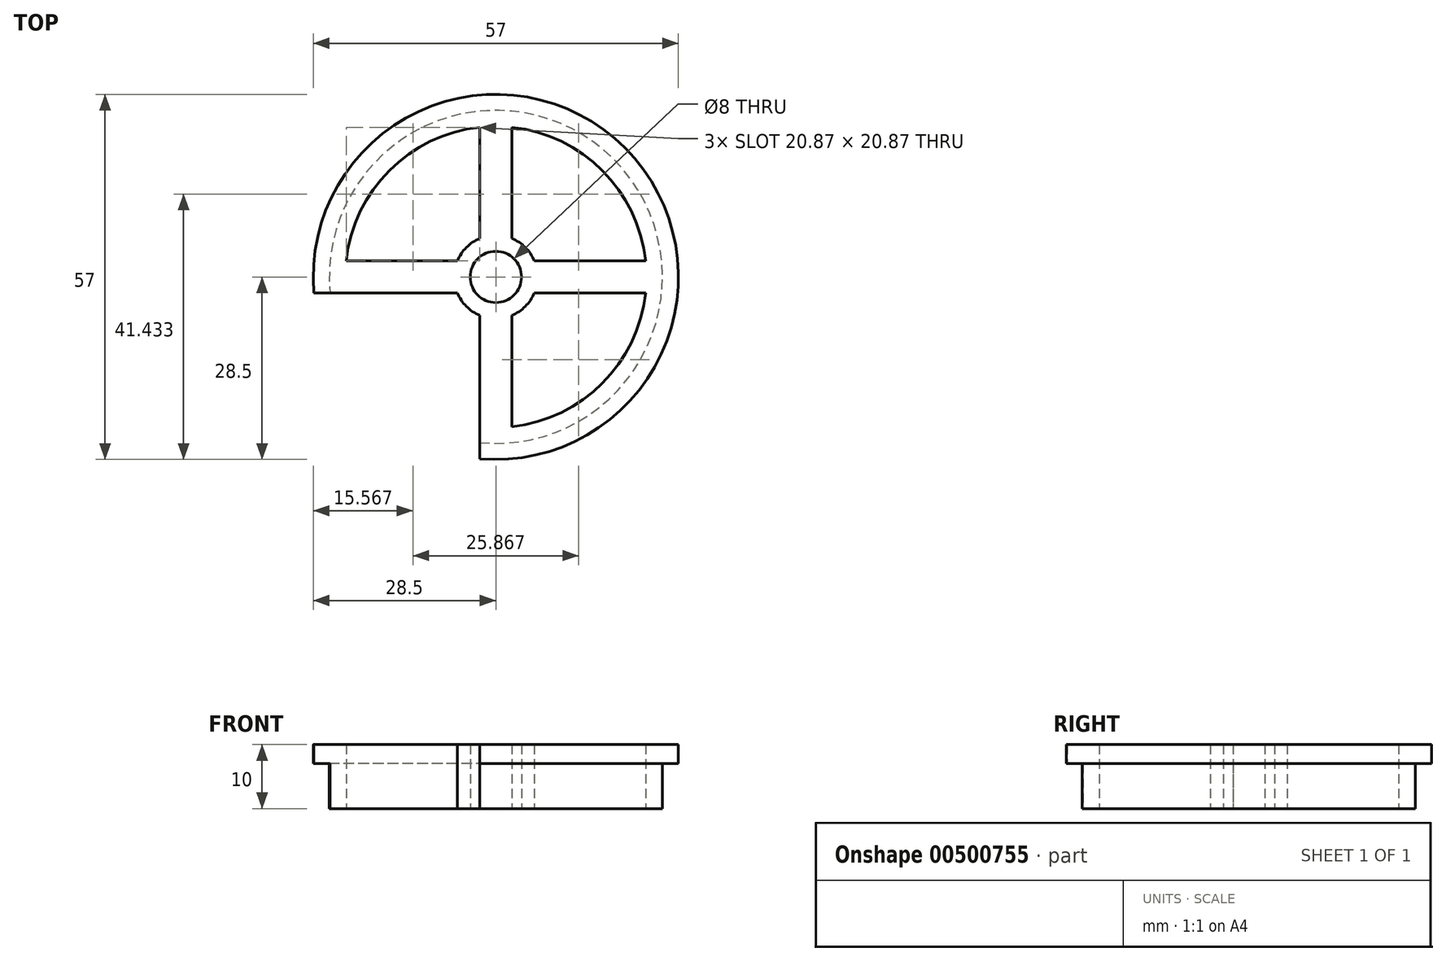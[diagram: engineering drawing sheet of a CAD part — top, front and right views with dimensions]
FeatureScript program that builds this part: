
annotation { "Feature Type Name" : "Feature", "Feature Type Description" : "" }
export const myFeature = defineFeature(function(context is Context, id is Id, definition is map)
    precondition{}
    {
        {
            var Q0;
            Q0=qCreatedBy(makeId("Top.planeOp"),FACE);
            var sketch = newSketch(context, id + "F0", { "sketchPlane" : qUnion([Q0])});
            skCircle(sketch, "E0", {"center": v(0, 0) * mm, "radius": 4 * mm});
            skCircle(sketch, "E1", {"center": v(0, 0) * mm, "radius": 26 * mm});
            skCircle(sketch, "E2", {"center": v(0, 0) * mm, "radius": 28.5 * mm});
            skCircle(sketch, "E3", {"center": v(0, 0) * mm, "radius": 6.5 * mm});
            skLineSegment(sketch, "E4.bottom", {"start": v(-2.5, 36.95) * mm, "end": v(2.5, 36.95) * mm});
            skLineSegment(sketch, "E4.top", {"start": v(-2.5, -38.22) * mm, "end": v(2.5, -38.22) * mm});
            skLineSegment(sketch, "E4.left", {"start": v(-2.5, 36.95) * mm, "end": v(-2.5, -38.22) * mm});
            skLineSegment(sketch, "E4.right", {"start": v(2.5, 36.95) * mm, "end": v(2.5, -38.22) * mm});
            skLineSegment(sketch, "E5.bottom", {"start": v(-35.79, 2.5) * mm, "end": v(49.49, 2.5) * mm});
            skLineSegment(sketch, "E5.top", {"start": v(-35.79, -2.5) * mm, "end": v(49.49, -2.5) * mm});
            skLineSegment(sketch, "E5.left", {"start": v(-35.79, 2.5) * mm, "end": v(-35.79, -2.5) * mm});
            skLineSegment(sketch, "E5.right", {"start": v(49.49, 2.5) * mm, "end": v(49.49, -2.5) * mm});
            skCircle(sketch, "E6", {"center": v(0, 0) * mm, "radius": 23.5 * mm});
            skSolve(sketch);
        }
        {
            var Q0;
            {var subQ0=sQuery(id+"F0.wireOp",EDGE,"E5.bottom");var subQ1=sQuery(id+"F0.wireOp",EDGE,"E1");var subQ2=makeQuery(id+"F0.imprint","INTERSECT",VERTEX,{"disambiguationData":[OD(0.0)],"derivedFrom":[subQ1,subQ0]});Q0=makeQuery(id+"F0.imprint","IMPRINT",FACE,{"disambiguationData":[TD([[makeQuery(id+"F0.imprint","IMPRINT",EDGE,{"disambiguationData":[TD([[subQ2,1.0]])],"derivedFrom":subQ1}),1.0]])]});}
            var Q1;
            {var subQ0=sQuery(id+"F0.wireOp",EDGE,"E5.bottom");var subQ1=sQuery(id+"F0.wireOp",EDGE,"E3");var subQ2=makeQuery(id+"F0.imprint","INTERSECT",VERTEX,{"disambiguationData":[OD(0.0)],"derivedFrom":[subQ1,subQ0]});Q1=makeQuery(id+"F0.imprint","IMPRINT",FACE,{"disambiguationData":[TD([[makeQuery(id+"F0.imprint","IMPRINT",EDGE,{"disambiguationData":[TD([[subQ2,1.0]])],"derivedFrom":subQ1}),-1.0]])]});}
            var Q2;
            {var subQ0=sQuery(id+"F0.wireOp",EDGE,"E4.right");var subQ1=sQuery(id+"F0.wireOp",EDGE,"E1");var subQ2=makeQuery(id+"F0.imprint","INTERSECT",VERTEX,{"disambiguationData":[OD(0.0)],"derivedFrom":[subQ1,subQ0]});Q2=makeQuery(id+"F0.imprint","IMPRINT",FACE,{"disambiguationData":[TD([[makeQuery(id+"F0.imprint","IMPRINT",EDGE,{"disambiguationData":[TD([[subQ2,1.0]])],"derivedFrom":subQ1}),1.0]])]});}
            var Q3;
            {var subQ0=sQuery(id+"F0.wireOp",EDGE,"E4.left");var subQ1=sQuery(id+"F0.wireOp",EDGE,"E1");var subQ2=makeQuery(id+"F0.imprint","INTERSECT",VERTEX,{"disambiguationData":[OD(0.0)],"derivedFrom":[subQ1,subQ0]});Q3=makeQuery(id+"F0.imprint","IMPRINT",FACE,{"disambiguationData":[TD([[makeQuery(id+"F0.imprint","IMPRINT",EDGE,{"disambiguationData":[TD([[subQ2,-1.0]])],"derivedFrom":subQ1}),1.0]])]});}
            var Q4;
            {var subQ0=sQuery(id+"F0.wireOp",EDGE,"E4.right");var subQ1=sQuery(id+"F0.wireOp",EDGE,"E1");var subQ2=makeQuery(id+"F0.imprint","INTERSECT",VERTEX,{"disambiguationData":[OD(0.0)],"derivedFrom":[subQ1,subQ0]});Q4=makeQuery(id+"F0.imprint","IMPRINT",FACE,{"disambiguationData":[TD([[makeQuery(id+"F0.imprint","IMPRINT",EDGE,{"disambiguationData":[TD([[subQ2,-1.0]])],"derivedFrom":subQ1}),1.0]])]});}
            var Q5;
            {var subQ0=sQuery(id+"F0.wireOp",EDGE,"E5.bottom");var subQ1=sQuery(id+"F0.wireOp",EDGE,"E1");var subQ2=makeQuery(id+"F0.imprint","INTERSECT",VERTEX,{"disambiguationData":[OD(1.0)],"derivedFrom":[subQ1,subQ0]});Q5=makeQuery(id+"F0.imprint","IMPRINT",FACE,{"disambiguationData":[TD([[makeQuery(id+"F0.imprint","IMPRINT",EDGE,{"disambiguationData":[TD([[subQ2,-1.0]])],"derivedFrom":subQ1}),1.0]])]});}
            var Q6;
            {var subQ0=sQuery(id+"F0.wireOp",EDGE,"E5.top");var subQ1=sQuery(id+"F0.wireOp",EDGE,"E1");var subQ2=makeQuery(id+"F0.imprint","INTERSECT",VERTEX,{"disambiguationData":[OD(0.0)],"derivedFrom":[subQ1,subQ0]});Q6=makeQuery(id+"F0.imprint","IMPRINT",FACE,{"disambiguationData":[TD([[makeQuery(id+"F0.imprint","IMPRINT",EDGE,{"disambiguationData":[TD([[subQ2,-1.0]])],"derivedFrom":subQ1}),1.0]])]});}
            var Q7;
            {var subQ0=sQuery(id+"F0.wireOp",EDGE,"E4.left");var subQ1=sQuery(id+"F0.wireOp",EDGE,"E1");var subQ2=makeQuery(id+"F0.imprint","INTERSECT",VERTEX,{"disambiguationData":[OD(1.0)],"derivedFrom":[subQ1,subQ0]});Q7=makeQuery(id+"F0.imprint","IMPRINT",FACE,{"disambiguationData":[TD([[makeQuery(id+"F0.imprint","IMPRINT",EDGE,{"disambiguationData":[TD([[subQ2,-1.0]])],"derivedFrom":subQ1}),1.0]])]});}
            var Q8;
            {var subQ0=sQuery(id+"F0.wireOp",EDGE,"E4.right");var subQ1=sQuery(id+"F0.wireOp",EDGE,"E1");var subQ2=makeQuery(id+"F0.imprint","INTERSECT",VERTEX,{"disambiguationData":[OD(1.0)],"derivedFrom":[subQ1,subQ0]});Q8=makeQuery(id+"F0.imprint","IMPRINT",FACE,{"disambiguationData":[TD([[makeQuery(id+"F0.imprint","IMPRINT",EDGE,{"disambiguationData":[TD([[subQ2,-1.0]])],"derivedFrom":subQ1}),1.0]])]});}
            var Q9;
            {var subQ0=sQuery(id+"F0.wireOp",EDGE,"E5.bottom");var subQ1=sQuery(id+"F0.wireOp",EDGE,"E3");var subQ2=makeQuery(id+"F0.imprint","INTERSECT",VERTEX,{"disambiguationData":[OD(1.0)],"derivedFrom":[subQ1,subQ0]});Q9=makeQuery(id+"F0.imprint","IMPRINT",FACE,{"disambiguationData":[TD([[makeQuery(id+"F0.imprint","IMPRINT",EDGE,{"disambiguationData":[TD([[subQ2,-1.0]])],"derivedFrom":subQ1}),-1.0]])]});}
            var Q10;
            {var subQ0=sQuery(id+"F0.wireOp",EDGE,"E4.left");var subQ1=sQuery(id+"F0.wireOp",EDGE,"E0");var subQ5=makeQuery(id+"F0.imprint","INTERSECT",VERTEX,{"disambiguationData":[OD(0.0)],"derivedFrom":[subQ1,subQ0]});Q10=makeQuery(id+"F0.imprint","IMPRINT",FACE,{"disambiguationData":[TD([[makeQuery(id+"F0.imprint","IMPRINT",EDGE,{"disambiguationData":[TD([[subQ5,-1.0]])],"derivedFrom":subQ1}),-1.0]])]});}
            var Q11;
            {var subQ3=sQuery(id+"F0.wireOp",EDGE,"E5.bottom");var subQ8=sQuery(id+"F0.wireOp",EDGE,"E0");var subQ9=makeQuery(id+"F0.imprint","INTERSECT",VERTEX,{"disambiguationData":[OD(0.0)],"derivedFrom":[subQ8,subQ3]});Q11=makeQuery(id+"F0.imprint","IMPRINT",FACE,{"disambiguationData":[TD([[makeQuery(id+"F0.imprint","IMPRINT",EDGE,{"disambiguationData":[TD([[subQ9,-1.0]])],"derivedFrom":subQ8}),-1.0]])]});}
            var Q12;
            {var subQ0=sQuery(id+"F0.wireOp",EDGE,"E4.left");var subQ1=sQuery(id+"F0.wireOp",EDGE,"E3");var subQ2=makeQuery(id+"F0.imprint","INTERSECT",VERTEX,{"disambiguationData":[OD(1.0)],"derivedFrom":[subQ1,subQ0]});Q12=makeQuery(id+"F0.imprint","IMPRINT",FACE,{"disambiguationData":[TD([[makeQuery(id+"F0.imprint","IMPRINT",EDGE,{"disambiguationData":[TD([[subQ2,-1.0]])],"derivedFrom":subQ1}),-1.0]])]});}
            var Q13;
            {var subQ0=sQuery(id+"F0.wireOp",EDGE,"E4.right");var subQ1=sQuery(id+"F0.wireOp",EDGE,"E0");var subQ9=makeQuery(id+"F0.imprint","INTERSECT",VERTEX,{"disambiguationData":[OD(0.0)],"derivedFrom":[subQ1,subQ0]});Q13=makeQuery(id+"F0.imprint","IMPRINT",FACE,{"disambiguationData":[TD([[makeQuery(id+"F0.imprint","IMPRINT",EDGE,{"disambiguationData":[TD([[subQ9,1.0]])],"derivedFrom":subQ1}),-1.0]])]});}
            var Q14;
            {var subQ0=sQuery(id+"F0.wireOp",EDGE,"E4.right");var subQ1=sQuery(id+"F0.wireOp",EDGE,"E3");var subQ2=makeQuery(id+"F0.imprint","INTERSECT",VERTEX,{"disambiguationData":[OD(1.0)],"derivedFrom":[subQ1,subQ0]});Q14=makeQuery(id+"F0.imprint","IMPRINT",FACE,{"disambiguationData":[TD([[makeQuery(id+"F0.imprint","IMPRINT",EDGE,{"disambiguationData":[TD([[subQ2,-1.0]])],"derivedFrom":subQ1}),1.0]])]});}
            var Q15;
            {var subQ3=sQuery(id+"F0.wireOp",EDGE,"E5.top");var subQ8=sQuery(id+"F0.wireOp",EDGE,"E0");var subQ9=makeQuery(id+"F0.imprint","INTERSECT",VERTEX,{"disambiguationData":[OD(0.0)],"derivedFrom":[subQ8,subQ3]});Q15=makeQuery(id+"F0.imprint","IMPRINT",FACE,{"disambiguationData":[TD([[makeQuery(id+"F0.imprint","IMPRINT",EDGE,{"disambiguationData":[TD([[subQ9,-1.0]])],"derivedFrom":subQ8}),-1.0]])]});}
            var Q16;
            {var subQ0=sQuery(id+"F0.wireOp",EDGE,"E5.top");var subQ1=sQuery(id+"F0.wireOp",EDGE,"E3");var subQ2=makeQuery(id+"F0.imprint","INTERSECT",VERTEX,{"disambiguationData":[OD(0.0)],"derivedFrom":[subQ1,subQ0]});Q16=makeQuery(id+"F0.imprint","IMPRINT",FACE,{"disambiguationData":[TD([[makeQuery(id+"F0.imprint","IMPRINT",EDGE,{"disambiguationData":[TD([[subQ2,-1.0]])],"derivedFrom":subQ1}),1.0]])]});}
            var Q17;
            {var subQ0=sQuery(id+"F0.wireOp",EDGE,"E4.left");var subQ1=sQuery(id+"F0.wireOp",EDGE,"E3");var subQ2=makeQuery(id+"F0.imprint","INTERSECT",VERTEX,{"disambiguationData":[OD(0.0)],"derivedFrom":[subQ1,subQ0]});Q17=makeQuery(id+"F0.imprint","IMPRINT",FACE,{"disambiguationData":[TD([[makeQuery(id+"F0.imprint","IMPRINT",EDGE,{"disambiguationData":[TD([[subQ2,-1.0]])],"derivedFrom":subQ1}),1.0]])]});}
            var Q18;
            {var subQ0=sQuery(id+"F0.wireOp",EDGE,"E4.right");var subQ1=sQuery(id+"F0.wireOp",EDGE,"E3");var subQ2=makeQuery(id+"F0.imprint","INTERSECT",VERTEX,{"disambiguationData":[OD(0.0)],"derivedFrom":[subQ1,subQ0]});Q18=makeQuery(id+"F0.imprint","IMPRINT",FACE,{"disambiguationData":[TD([[makeQuery(id+"F0.imprint","IMPRINT",EDGE,{"disambiguationData":[TD([[subQ2,1.0]])],"derivedFrom":subQ1}),1.0]])]});}
            var Q19;
            {var subQ0=sQuery(id+"F0.wireOp",EDGE,"E5.bottom");var subQ1=sQuery(id+"F0.wireOp",EDGE,"E0");var subQ2=makeQuery(id+"F0.imprint","INTERSECT",VERTEX,{"disambiguationData":[OD(0.0)],"derivedFrom":[subQ1,subQ0]});Q19=makeQuery(id+"F0.imprint","IMPRINT",FACE,{"disambiguationData":[TD([[makeQuery(id+"F0.imprint","IMPRINT",EDGE,{"disambiguationData":[TD([[subQ2,1.0]])],"derivedFrom":subQ1}),-1.0]])]});}
            var Q20;
            {var subQ0=sQuery(id+"F0.wireOp",EDGE,"E5.bottom");var subQ1=sQuery(id+"F0.wireOp",EDGE,"E0");var subQ2=makeQuery(id+"F0.imprint","INTERSECT",VERTEX,{"disambiguationData":[OD(1.0)],"derivedFrom":[subQ1,subQ0]});Q20=makeQuery(id+"F0.imprint","IMPRINT",FACE,{"disambiguationData":[TD([[makeQuery(id+"F0.imprint","IMPRINT",EDGE,{"disambiguationData":[TD([[subQ2,-1.0]])],"derivedFrom":subQ1}),-1.0]])]});}
            var Q21;
            {var subQ0=sQuery(id+"F0.wireOp",EDGE,"E4.left");var subQ1=sQuery(id+"F0.wireOp",EDGE,"E0");var subQ2=makeQuery(id+"F0.imprint","INTERSECT",VERTEX,{"disambiguationData":[OD(1.0)],"derivedFrom":[subQ1,subQ0]});Q21=makeQuery(id+"F0.imprint","IMPRINT",FACE,{"disambiguationData":[TD([[makeQuery(id+"F0.imprint","IMPRINT",EDGE,{"disambiguationData":[TD([[subQ2,-1.0]])],"derivedFrom":subQ1}),-1.0]])]});}
            var Q22;
            {var subQ0=sQuery(id+"F0.wireOp",EDGE,"E5.top");var subQ1=sQuery(id+"F0.wireOp",EDGE,"E0");var subQ2=makeQuery(id+"F0.imprint","INTERSECT",VERTEX,{"disambiguationData":[OD(1.0)],"derivedFrom":[subQ1,subQ0]});Q22=makeQuery(id+"F0.imprint","IMPRINT",FACE,{"disambiguationData":[TD([[makeQuery(id+"F0.imprint","IMPRINT",EDGE,{"disambiguationData":[TD([[subQ2,-1.0]])],"derivedFrom":subQ1}),-1.0]])]});}
            var Q23;
            {var subQ0=sQuery(id+"F0.wireOp",EDGE,"E4.right");var subQ1=sQuery(id+"F0.wireOp",EDGE,"E3");var subQ2=makeQuery(id+"F0.imprint","INTERSECT",VERTEX,{"disambiguationData":[OD(0.0)],"derivedFrom":[subQ1,subQ0]});Q23=makeQuery(id+"F0.imprint","IMPRINT",FACE,{"disambiguationData":[TD([[makeQuery(id+"F0.imprint","IMPRINT",EDGE,{"disambiguationData":[TD([[subQ2,-1.0]])],"derivedFrom":subQ1}),-1.0]])]});}
            var Q24;
            {var subQ0=sQuery(id+"F0.wireOp",EDGE,"E4.right");var subQ1=sQuery(id+"F0.wireOp",EDGE,"E0");var subQ2=makeQuery(id+"F0.imprint","INTERSECT",VERTEX,{"disambiguationData":[OD(0.0)],"derivedFrom":[subQ1,subQ0]});Q24=makeQuery(id+"F0.imprint","IMPRINT",FACE,{"disambiguationData":[TD([[makeQuery(id+"F0.imprint","IMPRINT",EDGE,{"disambiguationData":[TD([[subQ2,-1.0]])],"derivedFrom":subQ1}),-1.0]])]});}
            extrude(context, id + "F1", {"entities" : qUnion([Q0, Q1, Q2, Q3, Q4, Q5, Q6, Q7, Q8, Q9, Q10, Q11, Q12, Q13, Q14, Q15, Q16, Q17, Q18, Q19, Q20, Q21, Q22, Q23, Q24]), "depth" : 3 * mm, "hasSecondDirection" : true, "secondDirectionOppositeDirection" : true, "secondDirectionDepth" : 7 * mm});
        }
        {
            var Q0;
            {var subQ0=sQuery(id+"F0.wireOp",EDGE,"E4.right");var subQ1=sQuery(id+"F0.wireOp",EDGE,"E1");var subQ2=makeQuery(id+"F0.imprint","INTERSECT",VERTEX,{"disambiguationData":[OD(0.0)],"derivedFrom":[subQ1,subQ0]});Q0=makeQuery(id+"F0.imprint","IMPRINT",FACE,{"disambiguationData":[TD([[makeQuery(id+"F0.imprint","IMPRINT",EDGE,{"disambiguationData":[TD([[subQ2,1.0]])],"derivedFrom":subQ1}),-1.0]])]});}
            var Q1;
            {var subQ0=sQuery(id+"F0.wireOp",EDGE,"E4.right");var subQ1=sQuery(id+"F0.wireOp",EDGE,"E1");var subQ2=makeQuery(id+"F0.imprint","INTERSECT",VERTEX,{"disambiguationData":[OD(0.0)],"derivedFrom":[subQ1,subQ0]});Q1=makeQuery(id+"F0.imprint","IMPRINT",FACE,{"disambiguationData":[TD([[makeQuery(id+"F0.imprint","IMPRINT",EDGE,{"disambiguationData":[TD([[subQ2,-1.0]])],"derivedFrom":subQ1}),-1.0]])]});}
            var Q2;
            {var subQ0=sQuery(id+"F0.wireOp",EDGE,"E4.left");var subQ1=sQuery(id+"F0.wireOp",EDGE,"E1");var subQ2=makeQuery(id+"F0.imprint","INTERSECT",VERTEX,{"disambiguationData":[OD(0.0)],"derivedFrom":[subQ1,subQ0]});Q2=makeQuery(id+"F0.imprint","IMPRINT",FACE,{"disambiguationData":[TD([[makeQuery(id+"F0.imprint","IMPRINT",EDGE,{"disambiguationData":[TD([[subQ2,-1.0]])],"derivedFrom":subQ1}),-1.0]])]});}
            var Q3;
            {var subQ0=sQuery(id+"F0.wireOp",EDGE,"E5.bottom");var subQ1=sQuery(id+"F0.wireOp",EDGE,"E1");var subQ2=makeQuery(id+"F0.imprint","INTERSECT",VERTEX,{"disambiguationData":[OD(1.0)],"derivedFrom":[subQ1,subQ0]});Q3=makeQuery(id+"F0.imprint","IMPRINT",FACE,{"disambiguationData":[TD([[makeQuery(id+"F0.imprint","IMPRINT",EDGE,{"disambiguationData":[TD([[subQ2,-1.0]])],"derivedFrom":subQ1}),-1.0]])]});}
            var Q4;
            {var subQ0=sQuery(id+"F0.wireOp",EDGE,"E5.top");var subQ1=sQuery(id+"F0.wireOp",EDGE,"E1");var subQ2=makeQuery(id+"F0.imprint","INTERSECT",VERTEX,{"disambiguationData":[OD(0.0)],"derivedFrom":[subQ1,subQ0]});Q4=makeQuery(id+"F0.imprint","IMPRINT",FACE,{"disambiguationData":[TD([[makeQuery(id+"F0.imprint","IMPRINT",EDGE,{"disambiguationData":[TD([[subQ2,-1.0]])],"derivedFrom":subQ1}),-1.0]])]});}
            var Q5;
            {var subQ0=sQuery(id+"F0.wireOp",EDGE,"E4.left");var subQ1=sQuery(id+"F0.wireOp",EDGE,"E1");var subQ2=makeQuery(id+"F0.imprint","INTERSECT",VERTEX,{"disambiguationData":[OD(1.0)],"derivedFrom":[subQ1,subQ0]});Q5=makeQuery(id+"F0.imprint","IMPRINT",FACE,{"disambiguationData":[TD([[makeQuery(id+"F0.imprint","IMPRINT",EDGE,{"disambiguationData":[TD([[subQ2,-1.0]])],"derivedFrom":subQ1}),-1.0]])]});}
            var Q6;
            {var subQ0=sQuery(id+"F0.wireOp",EDGE,"E4.right");var subQ1=sQuery(id+"F0.wireOp",EDGE,"E1");var subQ2=makeQuery(id+"F0.imprint","INTERSECT",VERTEX,{"disambiguationData":[OD(1.0)],"derivedFrom":[subQ1,subQ0]});Q6=makeQuery(id+"F0.imprint","IMPRINT",FACE,{"disambiguationData":[TD([[makeQuery(id+"F0.imprint","IMPRINT",EDGE,{"disambiguationData":[TD([[subQ2,-1.0]])],"derivedFrom":subQ1}),-1.0]])]});}
            var Q7;
            {var subQ0=sQuery(id+"F0.wireOp",EDGE,"E5.bottom");var subQ1=sQuery(id+"F0.wireOp",EDGE,"E1");var subQ2=makeQuery(id+"F0.imprint","INTERSECT",VERTEX,{"disambiguationData":[OD(0.0)],"derivedFrom":[subQ1,subQ0]});Q7=makeQuery(id+"F0.imprint","IMPRINT",FACE,{"disambiguationData":[TD([[makeQuery(id+"F0.imprint","IMPRINT",EDGE,{"disambiguationData":[TD([[subQ2,1.0]])],"derivedFrom":subQ1}),-1.0]])]});}
            extrude(context, id + "F2", {"entities" : qUnion([Q0, Q1, Q2, Q3, Q4, Q5, Q6, Q7]), "operationType" : NewBodyOperationType.ADD, "depth" : 3 * mm});
        }
    });
